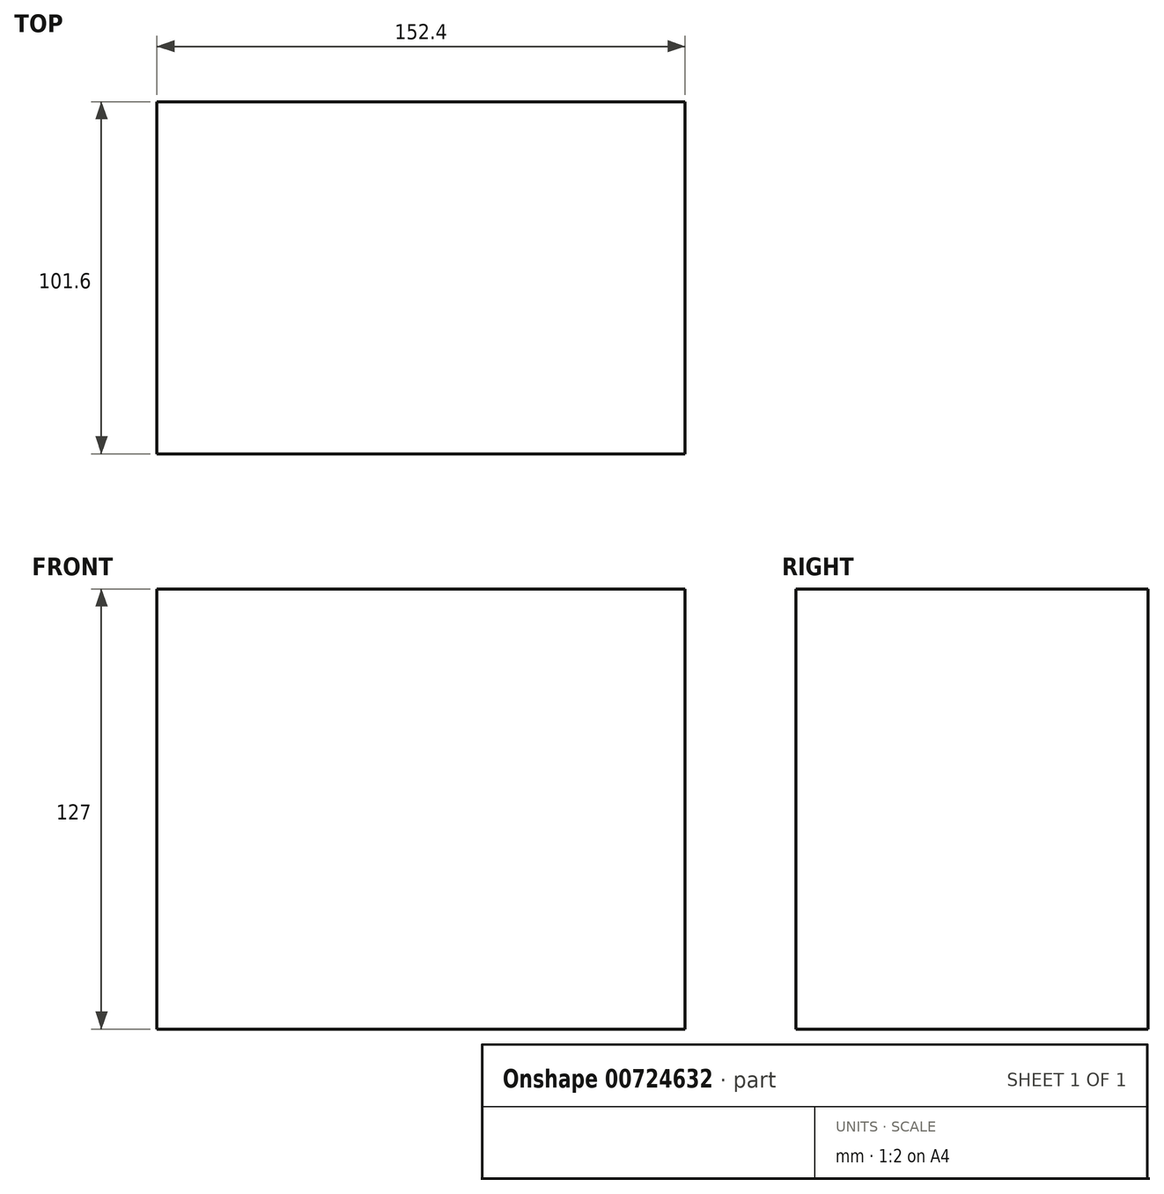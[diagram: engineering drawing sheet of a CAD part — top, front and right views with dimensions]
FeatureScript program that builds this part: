
annotation { "Feature Type Name" : "Feature", "Feature Type Description" : "" }
export const myFeature = defineFeature(function(context is Context, id is Id, definition is map)
    precondition{}
    {
        {
            var Q0;
            Q0=qCreatedBy(makeId("Front.planeOp"),FACE);
            var sketch = newSketch(context, id + "F0", { "sketchPlane" : qUnion([Q0])});
            skLineSegment(sketch, "E0", {"start": v(-75.78, -75.48) * mm, "end": v(-75.78, 51.52) * mm});
            skLineSegment(sketch, "E1", {"start": v(-75.78, 51.52) * mm, "end": v(76.62, 51.52) * mm});
            skLineSegment(sketch, "E2", {"start": v(76.62, 51.52) * mm, "end": v(76.62, -75.48) * mm});
            skLineSegment(sketch, "E3", {"start": v(76.62, -75.48) * mm, "end": v(-75.78, -75.48) * mm});
            skSolve(sketch);
        }
        {
            var Q0;
            Q0=makeQuery(id+"F0.imprint","IMPRINT",FACE,{"disambiguationData":[TD([[makeQuery(id+"F0.imprint","IMPRINT",EDGE,{"derivedFrom":sQuery(id+"F0.wireOp",EDGE,"E0")}),-1.0]])]});
            extrude(context, id + "F1", {"entities" : qUnion([Q0]), "depth" : 101.6 * mm, "offsetDistance" : 25.4 * mm});
        }
    });
